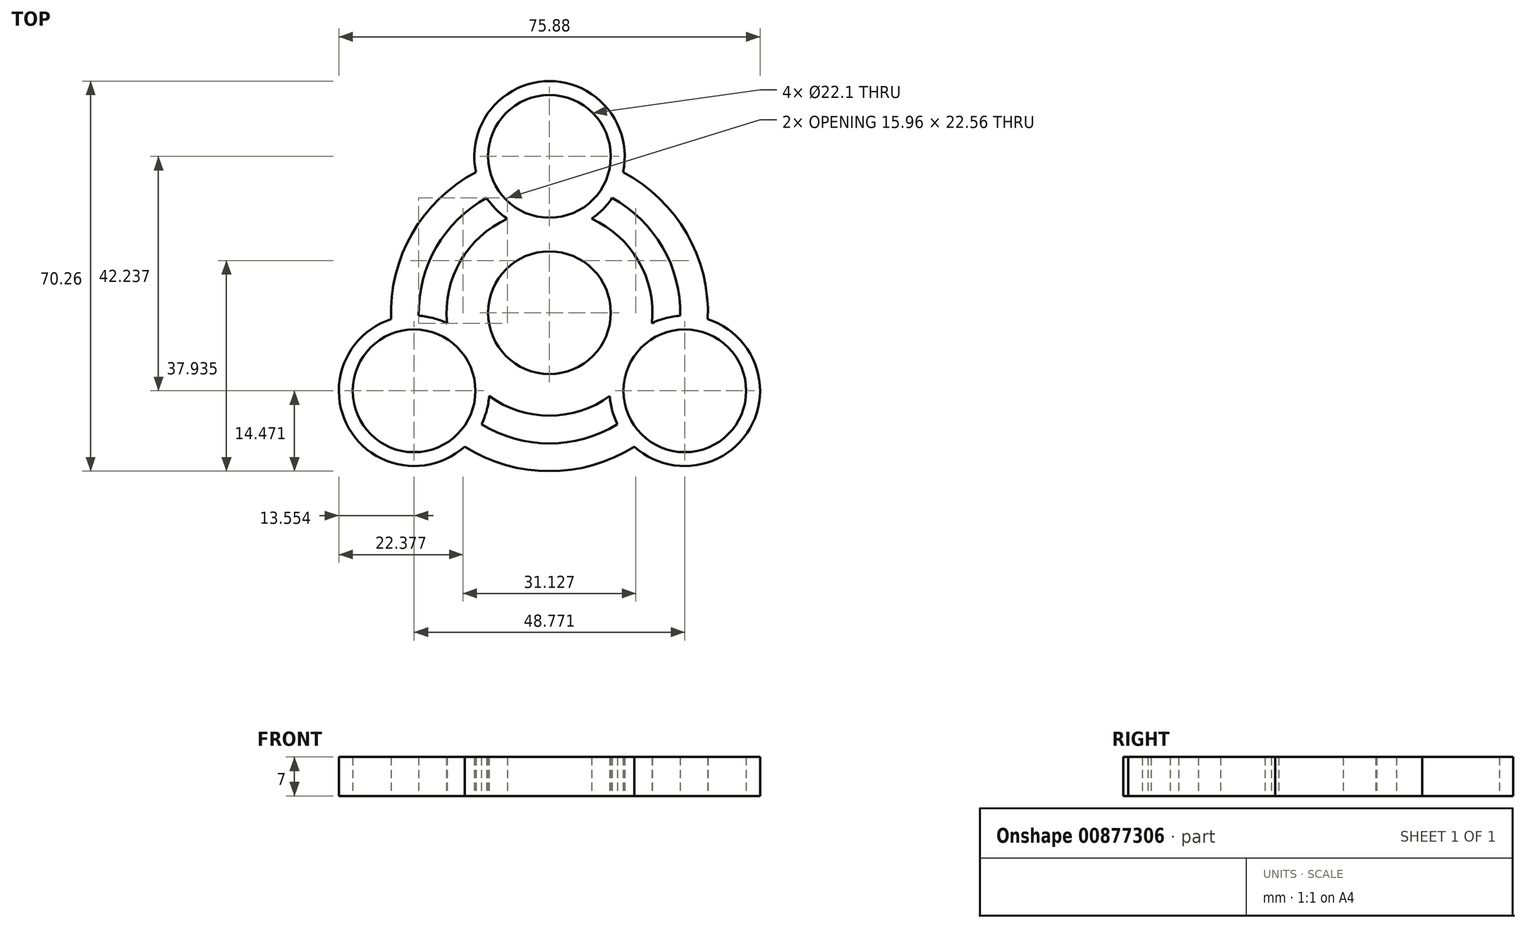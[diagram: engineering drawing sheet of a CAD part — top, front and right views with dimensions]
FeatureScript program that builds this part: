
annotation { "Feature Type Name" : "Feature", "Feature Type Description" : "" }
export const myFeature = defineFeature(function(context is Context, id is Id, definition is map)
    precondition{}
    {
        {
            var Q0;
            Q0=qCreatedBy(makeId("Top.planeOp"),FACE);
            var sketch = newSketch(context, id + "F0", { "sketchPlane" : qUnion([Q0])});
            skCircle(sketch, "E0", {"center": v(0, 0) * mm, "radius": 11.05 * mm});
            skCircle(sketch, "E1", {"center": v(0, 0) * mm, "radius": 13.55 * mm});
            skCircle(sketch, "E2", {"center": v(0, 28.16) * mm, "radius": 11.05 * mm});
            skArc(sketch, "E3", {"start": v(13.24, 25.3) * mm, "mid": v(0, 41.7) * mm, "end": v(-13.24, 25.3) * mm});
            skArc(sketch, "E4.1.0", {"start": v(-12.25, -20.11) * mm, "mid": v(-11.31, -17.64) * mm, "end": v(-10.87, -15.03) * mm});
            skCircle(sketch, "E4.1.1", {"center": v(-24.39, -14.08) * mm, "radius": 11.05 * mm});
            skArc(sketch, "E4.2.0", {"start": v(15.28, -24.12) * mm, "mid": v(36.12, -20.85) * mm, "end": v(28.53, -1.18) * mm});
            skCircle(sketch, "E4.2.1", {"center": v(24.39, -14.08) * mm, "radius": 11.05 * mm});
            skArc(sketch, "E5", {"start": v(-10.87, -15.03) * mm, "mid": v(0, -18.55) * mm, "end": v(10.87, -15.03) * mm});
            skArc(sketch, "E6", {"start": v(-12.25, -20.11) * mm, "mid": v(0, -23.55) * mm, "end": v(12.25, -20.11) * mm});
            skArc(sketch, "E7", {"start": v(-15.28, -24.12) * mm, "mid": v(0, -28.55) * mm, "end": v(15.28, -24.12) * mm});
            skArc(sketch, "E8.trimOffspring", {"start": v(-13.24, 25.3) * mm, "mid": v(-24.73, 14.28) * mm, "end": v(-28.53, -1.18) * mm});
            skArc(sketch, "E9.trimOffspring", {"start": v(-11.3, 20.67) * mm, "mid": v(-20.4, 11.78) * mm, "end": v(-23.54, -0.56) * mm});
            skArc(sketch, "E10.trimOffspring", {"start": v(-7.58, 16.93) * mm, "mid": v(-16.06, 9.28) * mm, "end": v(-18.45, -1.9) * mm});
            skArc(sketch, "E11.trimOffspring", {"start": v(18.45, -1.9) * mm, "mid": v(16.06, 9.28) * mm, "end": v(7.58, 16.93) * mm});
            skArc(sketch, "E12.trimOffspring", {"start": v(23.54, -0.56) * mm, "mid": v(20.4, 11.77) * mm, "end": v(11.3, 20.67) * mm});
            skArc(sketch, "E13.trimOffspring", {"start": v(28.53, -1.18) * mm, "mid": v(24.73, 14.27) * mm, "end": v(13.24, 25.3) * mm});
            skArc(sketch, "E14.trimOffspring", {"start": v(23.54, -0.56) * mm, "mid": v(20.93, -0.98) * mm, "end": v(18.45, -1.9) * mm});
            skArc(sketch, "E15.trimOffspring", {"start": v(-11.3, 20.67) * mm, "mid": v(-9.62, 18.62) * mm, "end": v(-7.58, 16.93) * mm});
            skArc(sketch, "E16.trimOffspring", {"start": v(-28.53, -1.18) * mm, "mid": v(-36.12, -20.85) * mm, "end": v(-15.28, -24.12) * mm});
            skArc(sketch, "E17.trimOffspring", {"start": v(10.87, -15.03) * mm, "mid": v(11.31, -17.64) * mm, "end": v(12.25, -20.11) * mm});
            skArc(sketch, "E18.trimOffspring", {"start": v(7.58, 16.93) * mm, "mid": v(9.62, 18.62) * mm, "end": v(11.3, 20.67) * mm});
            skArc(sketch, "E19.trimOffspring", {"start": v(-18.45, -1.9) * mm, "mid": v(-20.93, -0.98) * mm, "end": v(-23.54, -0.56) * mm});
            skSolve(sketch);
        }
        {
            var Q0;
            Q0=makeQuery(id+"F0.imprint","IMPRINT",FACE,{"disambiguationData":[TD([[makeQuery(id+"F0.imprint","IMPRINT",EDGE,{"derivedFrom":sQuery(id+"F0.wireOp",EDGE,"E1")}),-1.0]])]});
            var Q1;
            Q1=makeQuery(id+"F0.imprint","IMPRINT",FACE,{"disambiguationData":[TD([[makeQuery(id+"F0.imprint","IMPRINT",EDGE,{"derivedFrom":sQuery(id+"F0.wireOp",EDGE,"E0")}),-1.0]])]});
            extrude(context, id + "F1", {"entities" : qUnion([Q0, Q1]), "depth" : 7 * mm, "offsetDistance" : 25 * mm});
        }
    });
